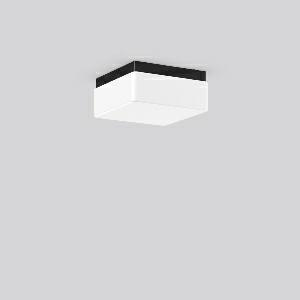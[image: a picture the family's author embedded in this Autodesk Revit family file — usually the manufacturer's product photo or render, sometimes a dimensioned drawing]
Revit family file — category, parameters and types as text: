
# Revit family: quadrat_21128_003_24ab
name_source: partatom
category: Lighting Fixtures
units: mm (PartAtom-declared; Revit-internal decimal feet)

## family parameters
Cut with Voids When Loaded = No
Host = Face
Light Source = No
Part Type = Normal
Room Calculation Point = No
Round Connector Dimension = Use Diameter
Shared = No

## types (1)
- QUADRAT (1 x QA60/clear E27, 915 lm, 57 W, 3000)
    Apparent Load = 57 VA
    CIE Flux Codes = 35 64 86 74 50
    Color Rendering = 90
    Color Temperature = 3000
    Default Elevation = 1800 mm
    Description = Series: QUADRAT
Square surface-mounted luminaire in classic design. Base: plastic. Opal glass: mouth-blown, satin finish. Diffuser fastening: spring system. Suitable for Ceiling mounting, Wall (surface). IP 43 ceiling mounting, IP 44 wall mounting. 
Colour: black
Length: 240 mm
Width: 240 mm
Height: 110 mm
Lamp: A60
Number of lamps: 1
Wattage: 75 W
Socket: E27
System power: 60 W
Rated luminous flux: 370 lm
Luminous efficiency: 6 lm/W
Control gear: Converter not necessary
Protection class: II
Type of protection: IP 43
    Height = 110 mm
    Lamp = 1 x QA60/clear E27
    Lamp Light Flux = 915 lm
    Lamp Power = 57 W
    Lamp count = 1
    Length = 240 mm
    Lifetime = 3000 h
    Luminous efficacy = 8 lm/W
    Manufacturer = RZB
    ModVariant = No
    Model = 21128.003
    Mounting Place = Ceiling
    Mounting Type = Surface mounted
    Number of Poles = 1
    OnlyDefault = Yes
    Power Factor = 1
    Product Name = QUADRAT
    Product group = Surface mounted ceiling and wall luminaires
    ProductGroupID = 305
    Protection Class = Protection class II
    Protection Degree = IP 43
    RLX_Detail_Level = 1
    RLX_Emergency_Light_Flux = 0 lm
    RLX_Emergency_Type = 0
    RLX_Emergency_Type_DB = No
    RlxData = <blob elided: 11597 chars, md5=9998b0c8>
    Socket = E27
    Standby Power = 0 W
    System Light Flux = 460 lm
    System Power = 57 W
    Type Comments = Product without accessories
    Type Image = 21128.003.jpg
    URL = http://relux.com
    VarID = ---
    Voltage = 0 V
    Weight = 0.00 kg
    Width = 240 mm

## geometry (parser evidence)
native form markers: Sweep x13
no freeform markers — native parametric forms only
